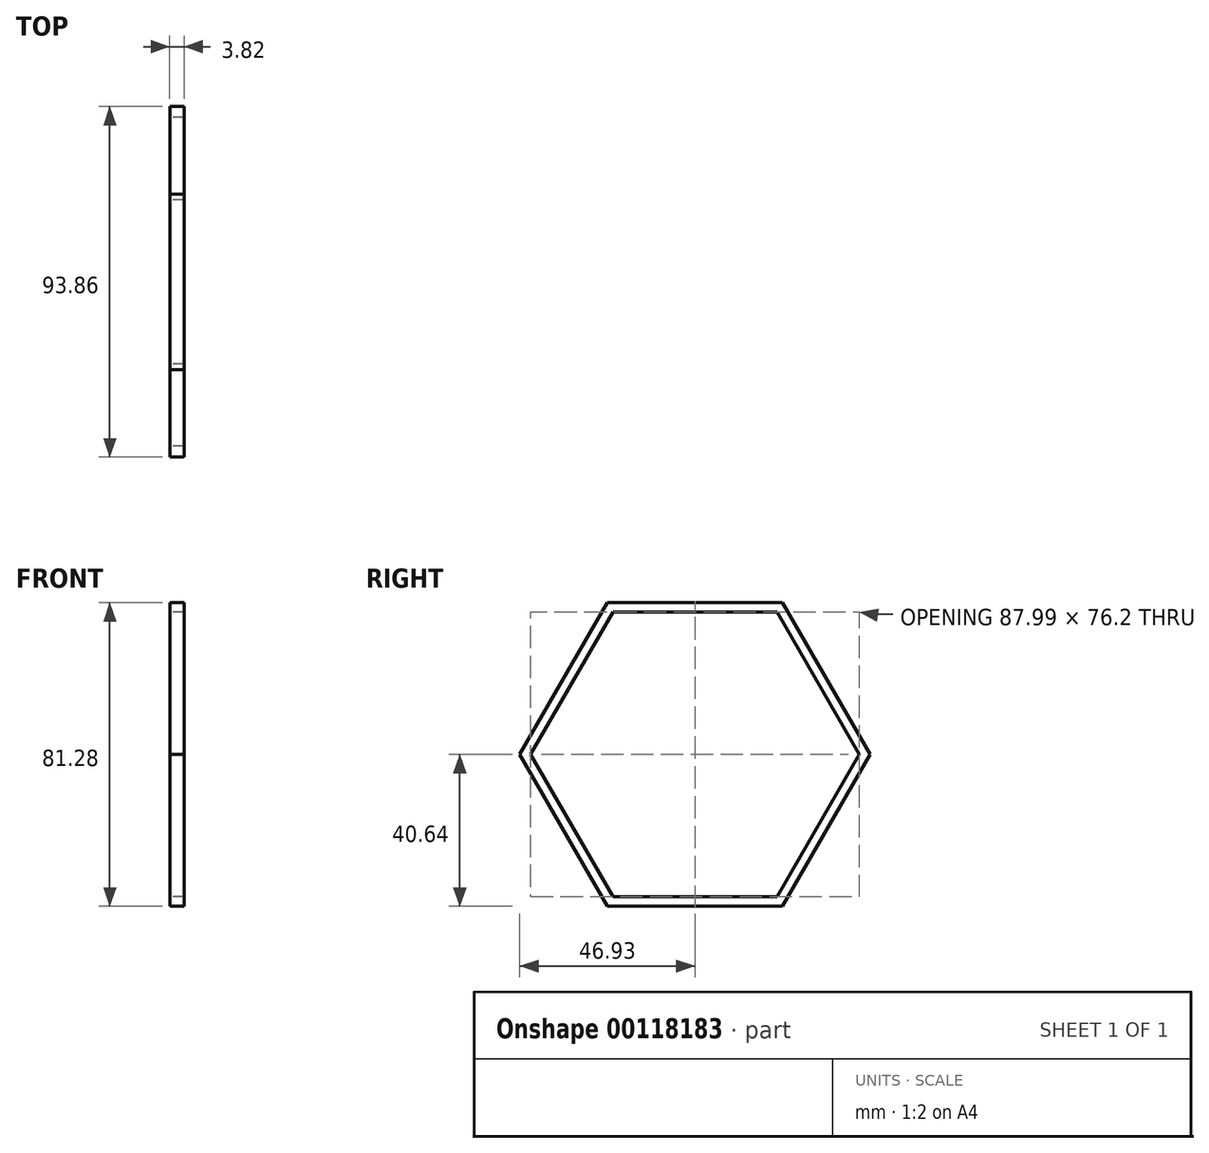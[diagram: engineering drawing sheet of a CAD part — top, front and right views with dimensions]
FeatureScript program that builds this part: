
annotation { "Feature Type Name" : "Feature", "Feature Type Description" : "" }
export const myFeature = defineFeature(function(context is Context, id is Id, definition is map)
    precondition{}
    {
        {
            var Q0;
            Q0=qCreatedBy(makeId("Right.planeOp"),FACE);
            var sketch = newSketch(context, id + "F0", { "sketchPlane" : qUnion([Q0])});
            skCircle(sketch, "E0.cCircle", {"center": v(0, 0) * mm, "radius": 38.1 * mm, "construction": true});
            skLineSegment(sketch, "E0.0", {"start": v(-22, 38.1) * mm, "end": v(22, 38.1) * mm});
            skLineSegment(sketch, "E0.1", {"start": v(22, 38.1) * mm, "end": v(44, 0) * mm});
            skLineSegment(sketch, "E0.2", {"start": v(44, 0) * mm, "end": v(22, -38.1) * mm});
            skLineSegment(sketch, "E0.3", {"start": v(22, -38.1) * mm, "end": v(-22, -38.1) * mm});
            skLineSegment(sketch, "E0.4", {"start": v(-22, -38.1) * mm, "end": v(-44, 0) * mm});
            skLineSegment(sketch, "E0.5", {"start": v(-44, 0) * mm, "end": v(-22, 38.1) * mm});
            skPoint(sketch, "E0.0.midPoint", {"position": v(0, 38.1) * mm});
            skLineSegment(sketch, "E1.0", {"start": v(-23.46, -40.64) * mm, "end": v(-46.93, 0) * mm});
            skLineSegment(sketch, "E1.1", {"start": v(-23.46, 40.64) * mm, "end": v(23.46, 40.64) * mm});
            skLineSegment(sketch, "E1.2", {"start": v(23.46, 40.64) * mm, "end": v(46.93, 0) * mm});
            skLineSegment(sketch, "E1.3", {"start": v(-46.93, 0) * mm, "end": v(-23.46, 40.64) * mm});
            skLineSegment(sketch, "E1.4", {"start": v(46.93, 0) * mm, "end": v(23.46, -40.64) * mm});
            skLineSegment(sketch, "E1.5", {"start": v(23.46, -40.64) * mm, "end": v(-23.46, -40.64) * mm});
            skSolve(sketch);
        }
        {
            var Q0;
            Q0=makeQuery(id+"F0.imprint","IMPRINT",FACE,{"disambiguationData":[TD([[makeQuery(id+"F0.imprint","IMPRINT",EDGE,{"derivedFrom":sQuery(id+"F0.wireOp",EDGE,"E0.0")}),1.0]])]});
            extrude(context, id + "F1", {"entities" : qUnion([Q0]), "endBound" : BoundingType.SYMMETRIC, "depth" : 3.8 * mm});
        }
    });
